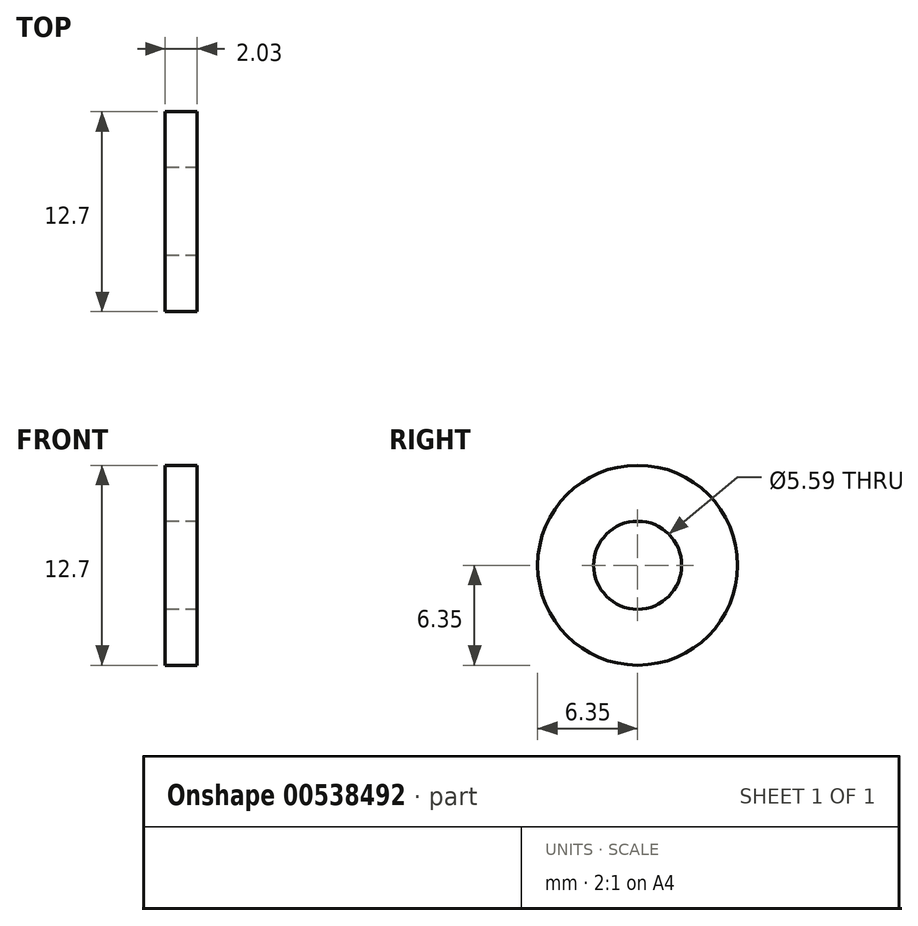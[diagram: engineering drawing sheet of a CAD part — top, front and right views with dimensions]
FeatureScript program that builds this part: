
annotation { "Feature Type Name" : "Feature", "Feature Type Description" : "" }
export const myFeature = defineFeature(function(context is Context, id is Id, definition is map)
    precondition{}
    {
        {
            var Q0;
            Q0=qCreatedBy(makeId("Right.planeOp"),FACE);
            var sketch = newSketch(context, id + "F0", { "sketchPlane" : qUnion([Q0])});
            skCircle(sketch, "E0", {"center": v(0, 0) * mm, "radius": 6.35 * mm});
            skCircle(sketch, "E1", {"center": v(0, 0) * mm, "radius": 2.8 * mm});
            skSolve(sketch);
        }
        {
            var Q0;
            Q0=makeQuery(id+"F0.imprint","IMPRINT",FACE,{"disambiguationData":[TD([[makeQuery(id+"F0.imprint","IMPRINT",EDGE,{"derivedFrom":sQuery(id+"F0.wireOp",EDGE,"E0")}),1.0]])]});
            extrude(context, id + "F1", {"entities" : qUnion([Q0]), "depth" : 2.03 * mm, "offsetDistance" : 25.4 * mm});
        }
    });
